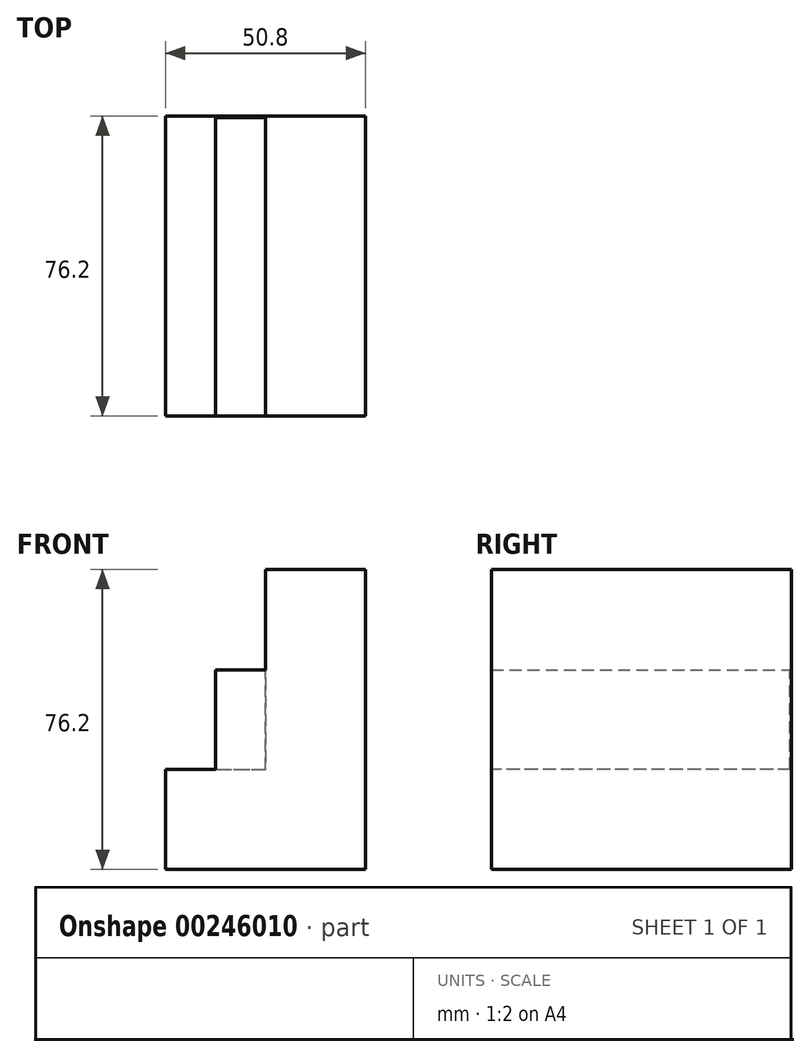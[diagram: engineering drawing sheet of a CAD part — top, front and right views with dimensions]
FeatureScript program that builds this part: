
annotation { "Feature Type Name" : "Feature", "Feature Type Description" : "" }
export const myFeature = defineFeature(function(context is Context, id is Id, definition is map)
    precondition{}
    {
        {
            var Q0;
            Q0=qCreatedBy(makeId("Top.planeOp"),FACE);
            var sketch = newSketch(context, id + "F0", { "sketchPlane" : qUnion([Q0])});
            skLineSegment(sketch, "E0.bottom", {"start": v(26.72, -26.04) * mm, "end": v(52.12, -26.04) * mm});
            skLineSegment(sketch, "E0.top", {"start": v(26.72, 50.16) * mm, "end": v(52.12, 50.16) * mm});
            skLineSegment(sketch, "E0.left", {"start": v(26.72, -26.04) * mm, "end": v(26.72, 50.16) * mm});
            skLineSegment(sketch, "E0.right", {"start": v(52.12, -26.04) * mm, "end": v(52.12, 50.16) * mm});
            skSolve(sketch);
        }
        {
            var Q0;
            Q0=makeQuery(id+"F0.imprint","IMPRINT",FACE,{"disambiguationData":[TD([[makeQuery(id+"F0.imprint","IMPRINT",EDGE,{"derivedFrom":sQuery(id+"F0.wireOp",EDGE,"E0.bottom")}),1.0]])]});
            extrude(context, id + "F1", {"entities" : qUnion([Q0]), "depth" : 76.2 * mm});
        }
        {
            var Q0;
            Q0=makeQuery(id+"F1.opExtrude","SWEPT_FACE",FACE,{"disambiguationData":[OSD([sQuery(id+"F0.wireOp",EDGE,"E0.left")])]});
            var sketch = newSketch(context, id + "F2", { "sketchPlane" : qUnion([Q0])});
            skLineSegment(sketch, "E1.bottom", {"start": v(-50.16, 0) * mm, "end": v(26.04, 0) * mm});
            skLineSegment(sketch, "E1.top", {"start": v(-50.16, 25.4) * mm, "end": v(26.04, 25.4) * mm});
            skLineSegment(sketch, "E1.left", {"start": v(-50.16, 0) * mm, "end": v(-50.16, 25.4) * mm});
            skLineSegment(sketch, "E1.right", {"start": v(26.04, 0) * mm, "end": v(26.04, 25.4) * mm});
            skSolve(sketch);
        }
        {
            var Q0;
            Q0=makeQuery(id+"F2.imprint","IMPRINT",FACE,{"disambiguationData":[TD([[makeQuery(id+"F2.imprint","IMPRINT",EDGE,{"derivedFrom":sQuery(id+"F2.wireOp",EDGE,"E1.bottom")}),-1.0]])]});
            extrude(context, id + "F3", {"entities" : qUnion([Q0]), "operationType" : NewBodyOperationType.ADD, "depth" : 25.4 * mm});
        }
        {
            var Q0;
            {var subQ0=sQuery(id+"F2.wireOp",EDGE,"E1.top");Q0=makeQuery(id+"F2.imprint","IMPRINT",FACE,{"disambiguationData":[TD([[makeQuery(id+"F2.imprint","IMPRINT",EDGE,{"derivedFrom":subQ0}),1.0]])]});}
            var sketch = newSketch(context, id + "F4", { "sketchPlane" : qUnion([Q0])});
            skLineSegment(sketch, "E2.bottom", {"start": v(26.42, 25.33) * mm, "end": v(-49.78, 25.33) * mm});
            skLineSegment(sketch, "E2.top", {"start": v(26.42, 50.73) * mm, "end": v(-49.78, 50.73) * mm});
            skLineSegment(sketch, "E2.left", {"start": v(26.42, 25.33) * mm, "end": v(26.42, 50.73) * mm});
            skLineSegment(sketch, "E2.right", {"start": v(-49.78, 25.33) * mm, "end": v(-49.78, 50.73) * mm});
            skSolve(sketch);
        }
        {
            var Q0;
            {var subQ0=sQuery(id+"F4.wireOp",EDGE,"E2.right");var subQ1=sQuery(id+"F4.wireOp",EDGE,"E2.top");var subQ2=makeQuery(id+"F4.imprint","INTERSECT",VERTEX,{"derivedFrom":[subQ1,subQ0]});Q0=makeQuery(id+"F4.imprint","IMPRINT",FACE,{"disambiguationData":[TD([[makeQuery(id+"F4.imprint","IMPRINT",EDGE,{"disambiguationData":[TD([[subQ2,1.0]])],"derivedFrom":subQ0}),-1.0]])]});}
            extrude(context, id + "F5", {"entities" : qUnion([Q0]), "operationType" : NewBodyOperationType.ADD, "depth" : 12.7 * mm});
        }
    });
